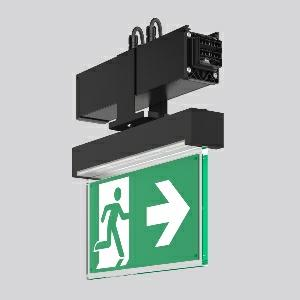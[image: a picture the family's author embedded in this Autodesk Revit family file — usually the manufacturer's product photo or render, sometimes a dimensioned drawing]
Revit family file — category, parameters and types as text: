
# Revit family: linedo_module_rz_9503rz_763_409_030_b7c1
name_source: partatom
category: Lighting Fixtures
units: mm (PartAtom-declared; Revit-internal decimal feet)

## family parameters
Cut with Voids When Loaded = No
Host = Face
Light Source = No
Part Type = Normal
Room Calculation Point = No
Round Connector Dimension = Use Diameter
Shared = No

## types (1)
- LINEDO Module RZ
    Apparent Load = 0 VA
    Default Elevation = 1800 mm
    Description = LINEDO, black, on/off
Continuous line luminaire, L 336 B 62 H 343, CBS, AC-Control
    Height = 343 mm
    Lamp = 0 x
    Length = 336 mm
    Luminous efficacy = 0 lm/W
    Manufacturer = RZB
    ModVariant = No
    Model = 9503RZ.763.409.030
    Mounting Place = Ceiling
    Mounting Type = Surface mounted
    Number of Poles = 1
    OnlyDefault = Yes
    Power Factor = 1
    Product Name = LINEDO Module RZ
    Product group = Continuous line luminaire system Linedo IP 54
    ProductGroupID = 314
    Protection Class = Protection class I
    Protection Degree = IP 54
    RLX_Detail_Level = 1
    RLX_Emergency_Light_Flux = 0 lm
    RLX_Emergency_Type = 0
    RLX_Emergency_Type_DB = No
    RlxData = <blob elided: 39865 chars, md5=d21679a9>
    Standby Power = 0 W
    System Light Flux = 0 lm
    System Power = 0 W
    Type Comments = Product without accessories
    Type Image = 9503rz.763.434.030.jpg
    URL = http://relux.com
    VarID = ---
    Voltage = 0 V
    Weight = 0.00 kg
    Width = 62 mm  [stored 0.203412 ft]

note: [stored X ft] marks values corroborated as IEEE doubles in the binary element streams (Revit-internal decimal feet)

## geometry (parser evidence)
native form markers: Blend x4, Sweep x14
no freeform markers — native parametric forms only
